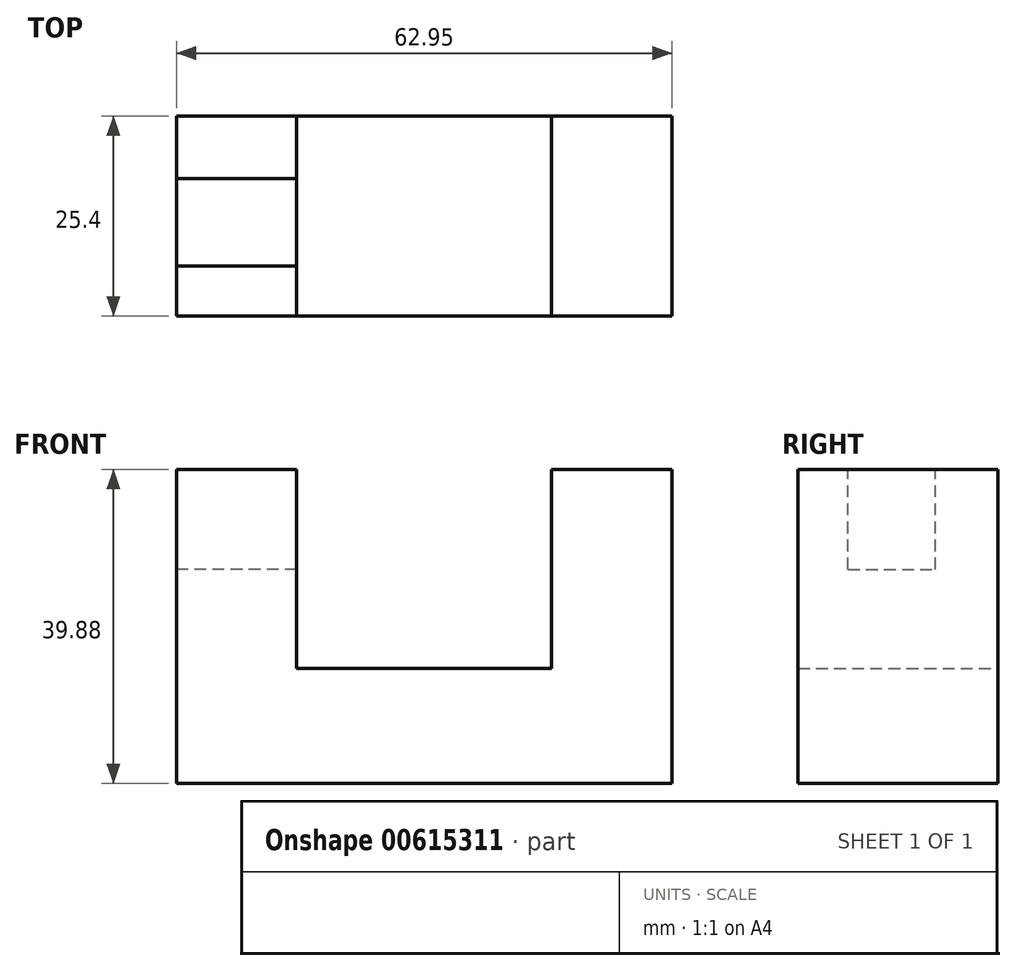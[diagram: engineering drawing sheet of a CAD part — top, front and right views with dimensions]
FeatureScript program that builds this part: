
annotation { "Feature Type Name" : "Feature", "Feature Type Description" : "" }
export const myFeature = defineFeature(function(context is Context, id is Id, definition is map)
    precondition{}
    {
        {
            var Q0;
            Q0=qCreatedBy(makeId("Front.planeOp"),FACE);
            var sketch = newSketch(context, id + "F0", { "sketchPlane" : qUnion([Q0])});
            skLineSegment(sketch, "E0.bottom", {"start": v(0, 0) * mm, "end": v(62.95, 0) * mm});
            skLineSegment(sketch, "E0.top", {"start": v(0, 39.88) * mm, "end": v(15.29, 39.88) * mm});
            skLineSegment(sketch, "E0.left", {"start": v(0, 0) * mm, "end": v(0, 39.88) * mm});
            skLineSegment(sketch, "E0.right", {"start": v(62.95, 0) * mm, "end": v(62.95, 39.88) * mm});
            skLineSegment(sketch, "E1.top", {"start": v(15.29, 14.61) * mm, "end": v(47.66, 14.61) * mm});
            skLineSegment(sketch, "E1.left", {"start": v(15.29, 39.88) * mm, "end": v(15.29, 14.61) * mm});
            skLineSegment(sketch, "E1.right", {"start": v(47.66, 39.88) * mm, "end": v(47.66, 14.61) * mm});
            skLineSegment(sketch, "E2.trimOffspring", {"start": v(47.66, 39.88) * mm, "end": v(62.95, 39.88) * mm});
            skSolve(sketch);
        }
        {
            var Q0;
            Q0=makeQuery(id+"F0.imprint","IMPRINT",FACE,{"disambiguationData":[TD([[makeQuery(id+"F0.imprint","IMPRINT",EDGE,{"derivedFrom":sQuery(id+"F0.wireOp",EDGE,"E0.bottom")}),1.0]])]});
            extrude(context, id + "F1", {"entities" : qUnion([Q0]), "depth" : 25.4 * mm, "offsetDistance" : 25.4 * mm});
        }
        {
            var Q0;
            Q0=makeQuery(id+"F1.opExtrude","SWEPT_FACE",FACE,{"disambiguationData":[OSD([sQuery(id+"F0.wireOp",EDGE,"E0.top")])]});
            var sketch = newSketch(context, id + "F2", { "sketchPlane" : qUnion([Q0])});
            skLineSegment(sketch, "E3.bottom", {"start": v(15.29, -7.92) * mm, "end": v(0, -7.92) * mm});
            skLineSegment(sketch, "E3.top", {"start": v(15.29, -19.05) * mm, "end": v(0, -19.05) * mm});
            skLineSegment(sketch, "E3.left", {"start": v(15.29, -7.92) * mm, "end": v(15.29, -19.05) * mm});
            skLineSegment(sketch, "E3.right", {"start": v(0, -7.92) * mm, "end": v(0, -19.05) * mm});
            skSolve(sketch);
        }
        {
            var Q0;
            Q0=makeQuery(id+"F2.imprint","IMPRINT",FACE,{"disambiguationData":[TD([[makeQuery(id+"F2.imprint","IMPRINT",EDGE,{"derivedFrom":sQuery(id+"F2.wireOp",EDGE,"E3.bottom")}),1.0]])]});
            extrude(context, id + "F3", {"entities" : qUnion([Q0]), "operationType" : NewBodyOperationType.REMOVE, "oppositeDirection" : true, "depth" : 12.7 * mm, "offsetDistance" : 25.4 * mm});
        }
    });
